# Revit family: LDA_BIM_PANEL EMERGENCIA_VAP-1
name_source: partatom
category: Equipos especializados
units: mm (PartAtom-declared; Revit-internal decimal feet)

## family parameters
Compartido = No
Corte con vacíos al cargar = No
Cota de conector redondo = Diámetro de uso
Punto de cálculo de habitación = No
Se basa en plano de trabajo = No
Siempre vertical = Sí
Tipo de pieza = Normal

## types (1)
- LDA_BIM_PANEL EMERGENCIA_VAP-1
    Acabado = Fe, Gris RAL 7016
    Accesorios Teclado Extensión = 1 x adaptador puerto de expansión 2 x 5 contactos macho-macho // 1 x Accesorio de unión a VAP 1 // 4 x Tornillos avellandados 4 x 8 mm
    Accesorios VAP-1 = 1 x cable miniUSB AB macho a USB A macho//1x Fuente de alimentación USB conector Tipo C(EU)//1 x Cable Ethernet 2m / 6,56ft.//2 x Alas para fijación en Rack de 19”//1 x accesorio de bloqueo instalación mural
    Alimentación = 4.5- 5.5V DC, 1 x miniUSB tipo AB
    Botones = Energencia, Reset, Confirmación, (EMG, RST, ACK), 1 botón Hablar (TALK), Mensajes grabados: Evacuación y Alerta, Test de indicadores
    Bus ACSI = 2 x Puertos ACSI idénticos: Audio Balanceado 1Vp, 0,707Vrms. 10 KKΩ, RJ-45 hembra, Total 1000m. / 3280ft
    Condiciones de Funcionamiento = 5 ºC to +45 ºC / 23 ºF to 113 ºF // 5% to 95% Humedad Relativa (sin condensación)
    Consumo Teclado Expansión = 40 mA max
    Consumo VAP-1 = 200 - 500 mA (max con todos los teclados de expansión)
    DPS = Integrado. 48 kHz, 24 bits - 172 MIPS
    Descripción = El panel de alarma por voz VAP-1 esta diseñado para dotar al sistema NEO de controles para el sistema de evacuación en diferentes ubicaciones.
    Dimensiones con micro (A x H x P) = 259mm x 132mm x 93mm / 3,38” x 2,56” x 7,48”
    Dimensiones sin micro (A x H x P) = 259mm x 132mm x 50mm / 3,38” x 2,56” x 7,48”
    Dimensiones teclado expansión/Complementos para rack (A x H x P) = 86mm x 132mm x 42mm / 3,38” x 2,56” x 7,48”
    Direccionalidad = Axial con diagrama hiperrcardioide
    Elevación por defecto = 0 mm  [stored 0 ft]
    Fabricante = LDA
    Funciones = Tono de preaviso, control de volumen, DSA (Ajuste dinámico de sonido). Direccionamiento de hasta 448 zonas del sistema.
    Indicadores = Estado: Emergencia, Fallo General, Remote Control // Fallo: Enlace, Alimentación, Micrófono de Emergencia // Mensaje en emisión: Grabado de Evacuación, Grabado de Alerta, Mensaje en vivo
    Longitud cable Micrófono = 500mm / 13,75"
    Modelo = VAP-1
    Peso = 1 Kg
    Peso Teclado Expansión = 0,5 Kg
    Puerto de expansión = 1 x Tira de pines 2 filas x 5 contactos hembra
    Referencia = LDAVAP1S02
    Relación Señal a Ruido = >98 dB, ponderación A
    Respuesta en frecuencia = 200 Hz – 12000 Hz (+/- 2dB)
    Sensibilidad = -43 dB (1KHz)
    Tipo de transductor = Dinámico de bobina móvil
    URL = https://support.lda-audiotech.com

note: [stored X ft] marks values corroborated as IEEE doubles in the binary element streams (Revit-internal decimal feet)

## geometry (parser evidence)
native form markers: Sweep x2
no freeform markers — native parametric forms only
